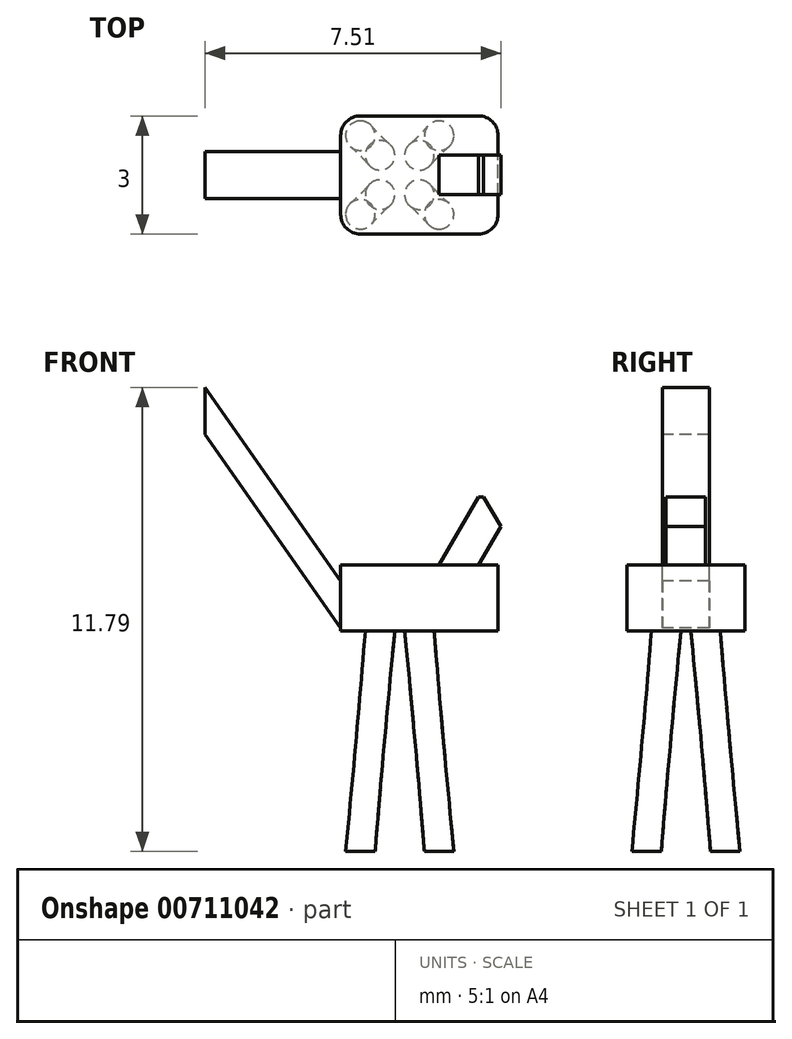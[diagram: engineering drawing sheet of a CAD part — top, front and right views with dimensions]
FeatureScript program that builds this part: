
annotation { "Feature Type Name" : "Feature", "Feature Type Description" : "" }
export const myFeature = defineFeature(function(context is Context, id is Id, definition is map)
    precondition{}
    {
        {
            var Q0;
            Q0=qCreatedBy(makeId("Top.planeOp"),FACE);
            var sketch = newSketch(context, id + "F0", { "sketchPlane" : qUnion([Q0])});
            skCircle(sketch, "E0", {"center": v(1, -1) * mm, "radius": 0.38 * mm});
            skLineSegment(sketch, "E1.bottom", {"start": v(1, -1) * mm, "end": v(-1, -1) * mm, "construction": true});
            skLineSegment(sketch, "E1.top", {"start": v(1, 1) * mm, "end": v(-1, 1) * mm, "construction": true});
            skLineSegment(sketch, "E1.left", {"start": v(1, -1) * mm, "end": v(1, 1) * mm, "construction": true});
            skLineSegment(sketch, "E1.right", {"start": v(-1, -1) * mm, "end": v(-1, 1) * mm, "construction": true});
            skCircle(sketch, "E2", {"center": v(-1, -1) * mm, "radius": 0.38 * mm});
            skCircle(sketch, "E3", {"center": v(-1, 1) * mm, "radius": 0.38 * mm});
            skCircle(sketch, "E4", {"center": v(1, 1) * mm, "radius": 0.38 * mm});
            skSolve(sketch);
        }
        {
            var Q0;
            Q0=qCreatedBy(makeId("Top.planeOp"),FACE);
            cPlane(context, id + "F1", {"entities" : qUnion([Q0]), "cplaneType" : CPlaneType.OFFSET, "offset" : (10 * .56) * mm, "width" : 150 * mm, "height" : 150 * mm});
        }
        {
            var Q0;
            Q0=qCreatedBy(makeId("Right.planeOp"),FACE);
            var sketch = newSketch(context, id + "F2", { "sketchPlane" : qUnion([Q0])});
            skLineSegment(sketch, "E5", {"start": v(0, 0) * mm, "end": v(0, 20.9) * mm, "construction": true});
            skSolve(sketch);
        }
        {
            var Q0;
            Q0=qCreatedBy(id+"F1.planeOp",FACE);
            var sketch = newSketch(context, id + "F3", { "sketchPlane" : qUnion([Q0])});
            skLineSegment(sketch, "E6.bottom", {"start": v(-0.5, 0.5) * mm, "end": v(0.5, 0.5) * mm, "construction": true});
            skLineSegment(sketch, "E6.top", {"start": v(-0.5, -0.5) * mm, "end": v(0.5, -0.5) * mm, "construction": true});
            skLineSegment(sketch, "E6.left", {"start": v(-0.5, 0.5) * mm, "end": v(-0.5, -0.5) * mm, "construction": true});
            skLineSegment(sketch, "E6.right", {"start": v(0.5, 0.5) * mm, "end": v(0.5, -0.5) * mm, "construction": true});
            skCircle(sketch, "E7", {"center": v(-0.5, 0.5) * mm, "radius": 0.38 * mm});
            skCircle(sketch, "E8", {"center": v(0.5, 0.5) * mm, "radius": 0.38 * mm});
            skCircle(sketch, "E9", {"center": v(-0.5, -0.5) * mm, "radius": 0.38 * mm});
            skCircle(sketch, "E10", {"center": v(0.5, -0.5) * mm, "radius": 0.38 * mm});
            skLineSegment(sketch, "E11.bottom", {"start": v(-1, 1) * mm, "end": v(1, 1) * mm});
            skLineSegment(sketch, "E11.top", {"start": v(-1, -1) * mm, "end": v(1, -1) * mm});
            skLineSegment(sketch, "E11.left", {"start": v(-1, 1) * mm, "end": v(-1, -1) * mm});
            skLineSegment(sketch, "E11.right", {"start": v(1, 1) * mm, "end": v(1, -1) * mm});
            skSolve(sketch);
        }
        {
            var Q0;
            Q0=makeQuery(id+"F0.imprint","IMPRINT",FACE,{"disambiguationData":[TD([[makeQuery(id+"F0.imprint","IMPRINT",EDGE,{"derivedFrom":sQuery(id+"F0.wireOp",EDGE,"E4")}),1.0]])]});
            var Q1;
            Q1=makeQuery(id+"F3.imprint","IMPRINT",FACE,{"disambiguationData":[TD([[makeQuery(id+"F3.imprint","IMPRINT",EDGE,{"derivedFrom":sQuery(id+"F3.wireOp",EDGE,"E8")}),1.0]])]});
            loft(context, id + "F4", {"sheetProfilesArray" : [{ "sheetProfileEntities" : qUnion([Q0]) }, { "sheetProfileEntities" : qUnion([Q1]) }]});
        }
        {
            var Q0;
            Q0=makeQuery(id+"F4.opLoft","SWEPT_BODY",BODY,{"disambiguationData":[OSD([makeQuery(id+"F0.imprint","IMPRINT",FACE,{"disambiguationData":[TD([[makeQuery(id+"F0.imprint","IMPRINT",EDGE,{"derivedFrom":sQuery(id+"F0.wireOp",EDGE,"E4")}),1.0]])]}),makeQuery(id+"F3.imprint","IMPRINT",FACE,{"disambiguationData":[TD([[makeQuery(id+"F3.imprint","IMPRINT",EDGE,{"derivedFrom":sQuery(id+"F3.wireOp",EDGE,"E8")}),1.0]])]})])]});
            var Q1;
            Q1=sQuery(id+"F2.wireOp",EDGE,"E5");
            circularPattern(context, id + "F5", {"entities" : qUnion([Q0]), "axis" : qUnion([Q1]), "angle" : 360 * degree, "instanceCount" : 4, "equalSpace" : true});
        }
        {
            var Q0;
            Q0=qCreatedBy(id+"F1.planeOp",FACE);
            var sketch = newSketch(context, id + "F6", { "sketchPlane" : qUnion([Q0])});
            skLineSegment(sketch, "E12.bottom", {"start": v(2, -1.5) * mm, "end": v(-1, -1.5) * mm});
            skLineSegment(sketch, "E12.top", {"start": v(2, 1.5) * mm, "end": v(-1, 1.5) * mm});
            skLineSegment(sketch, "E12.left", {"start": v(2.5, -1) * mm, "end": v(2.5, 1) * mm});
            skLineSegment(sketch, "E12.right", {"start": v(-1.5, -1) * mm, "end": v(-1.5, 1) * mm});
            skLineSegment(sketch, "E13", {"start": v(0, 0) * mm, "end": v(-1.5, 0) * mm, "construction": true});
            skLineSegment(sketch, "E14", {"start": v(0, 0) * mm, "end": v(0, -1.5) * mm, "construction": true});
            skPoint(sketch, "E15.visualSharp", {"position": v(-1.5, -1.5) * mm});
            skArc(sketch, "E15.filletArc", {"start": v(-1.5, -1) * mm, "mid": v(-1.35, -1.35) * mm, "end": v(-1, -1.5) * mm});
            skPoint(sketch, "E16.visualSharp", {"position": v(-1.5, 1.5) * mm});
            skArc(sketch, "E16.filletArc", {"start": v(-1, 1.5) * mm, "mid": v(-1.35, 1.35) * mm, "end": v(-1.5, 1) * mm});
            skPoint(sketch, "E17.visualSharp", {"position": v(2.5, 1.5) * mm});
            skArc(sketch, "E17.filletArc", {"start": v(2.5, 1) * mm, "mid": v(2.35, 1.35) * mm, "end": v(2, 1.5) * mm});
            skPoint(sketch, "E18.visualSharp", {"position": v(2.5, -1.5) * mm});
            skArc(sketch, "E18.filletArc", {"start": v(2, -1.5) * mm, "mid": v(2.35, -1.35) * mm, "end": v(2.5, -1) * mm});
            skSolve(sketch);
        }
        {
            var Q0;
            Q0=qSketchRegion(id+"F6",true);
            var Q1;
            Q1=sQuery(id+"F6.wireOp",EDGE,"E12.right");
            var Q2;
            Q2=sQuery(id+"F6.wireOp",EDGE,"E12.left");
            var Q3;
            Q3=sQuery(id+"F6.wireOp",EDGE,"E12.top");
            var Q4;
            Q4=sQuery(id+"F6.wireOp",EDGE,"E12.bottom");
            extrude(context, id + "F7", {"entities" : qUnion([Q0]), "surfaceEntities" : qUnion([Q1, Q2, Q3, Q4]), "depth" : (3 * .56) * mm, "offsetDistance" : 25 * mm});
        }
        {
            var Q0;
            Q0=qCreatedBy(makeId("Front.planeOp"),FACE);
            var sketch = newSketch(context, id + "F8", { "sketchPlane" : qUnion([Q0])});
            skLineSegment(sketch, "E19", {"start": v(-1.5, 6.28) * mm, "end": v(-4.94, 11.2) * mm});
            skSolve(sketch);
        }
        {
            var Q0;
            Q0=makeQuery(id+"F7.opExtrude","SWEPT_FACE",FACE,{"disambiguationData":[OSD([sQuery(id+"F6.wireOp",EDGE,"E12.right")])]});
            var sketch = newSketch(context, id + "F9", { "sketchPlane" : qUnion([Q0])});
            skLineSegment(sketch, "E20.bottom", {"start": v(-0.6, 6.88) * mm, "end": v(0.6, 6.88) * mm});
            skLineSegment(sketch, "E20.top", {"start": v(-0.6, 5.68) * mm, "end": v(0.6, 5.68) * mm});
            skLineSegment(sketch, "E20.left", {"start": v(-0.6, 6.88) * mm, "end": v(-0.6, 5.68) * mm});
            skLineSegment(sketch, "E20.right", {"start": v(0.6, 6.88) * mm, "end": v(0.6, 5.68) * mm});
            skSolve(sketch);
        }
        {
            var Q0;
            Q0=qSketchRegion(id+"F9",true);
            var Q1;
            Q1=qConstructionFilter(qBodyType(qCreatedBy(id+"F8",EDGE),BodyType.WIRE),ConstructionObject.NO);
            sweep(context, id + "F10", {"operationType" : NewBodyOperationType.ADD, "profiles" : qUnion([Q0]), "path" : qUnion([Q1])});
        }
        {
            var Q0;
            Q0=makeQuery(id+"F7.opExtrude","CAP_FACE",FACE,{"disambiguationData":[OSD([sQuery(id+"F6.wireOp",EDGE,"E12.bottom"),sQuery(id+"F6.wireOp",EDGE,"E12.top"),sQuery(id+"F6.wireOp",EDGE,"E12.left"),sQuery(id+"F6.wireOp",EDGE,"E12.right"),sQuery(id+"F6.wireOp",EDGE,"E15.filletArc"),sQuery(id+"F6.wireOp",EDGE,"E16.filletArc"),sQuery(id+"F6.wireOp",EDGE,"E17.filletArc"),sQuery(id+"F6.wireOp",EDGE,"E18.filletArc")])],"isStart":false});
            var sketch = newSketch(context, id + "F11", { "sketchPlane" : qUnion([Q0])});
            skLineSegment(sketch, "E21.bottom", {"start": v(2, -0.5) * mm, "end": v(1, -0.5) * mm});
            skLineSegment(sketch, "E21.top", {"start": v(2, 0.5) * mm, "end": v(1, 0.5) * mm});
            skLineSegment(sketch, "E21.left", {"start": v(2, -0.5) * mm, "end": v(2, 0.5) * mm});
            skLineSegment(sketch, "E21.right", {"start": v(1, -0.5) * mm, "end": v(1, 0.5) * mm});
            skSolve(sketch);
        }
        {
            var Q0;
            Q0=qCreatedBy(makeId("Front.planeOp"),FACE);
            var sketch = newSketch(context, id + "F12", { "sketchPlane" : qUnion([Q0])});
            skLineSegment(sketch, "E22", {"start": v(1.5, 7.32) * mm, "end": v(2.5, 9.05) * mm});
            skLineSegment(sketch, "E23", {"start": v(1.5, 7.32) * mm, "end": v(0, 7.32) * mm});
            skSolve(sketch);
        }
        {
            var Q0;
            Q0=makeQuery(id+"F11.imprint","IMPRINT",FACE,{"disambiguationData":[TD([[makeQuery(id+"F11.imprint","IMPRINT",EDGE,{"derivedFrom":sQuery(id+"F11.wireOp",EDGE,"E21.bottom")}),-1.0]])]});
            var Q1;
            Q1=sQuery(id+"F12.wireOp",EDGE,"E22");
            sweep(context, id + "F13", {"operationType" : NewBodyOperationType.ADD, "profiles" : qUnion([Q0]), "path" : qUnion([Q1])});
        }
        {
            var Q0;
            Q0=makeQuery(id+"F13.opSweep","CAP_EDGE",EDGE,{"disambiguationData":[OSD([sQuery(id+"F11.wireOp",EDGE,"E21.left"),sQuery(id+"F12.wireOp",VERTEX,"E22.end")])],"isStart":false});
            chamfer(context, id + "F14", {"entities" : qUnion([Q0]), "width" : .5 * mm, "tangentPropagation" : true});
        }
    });
